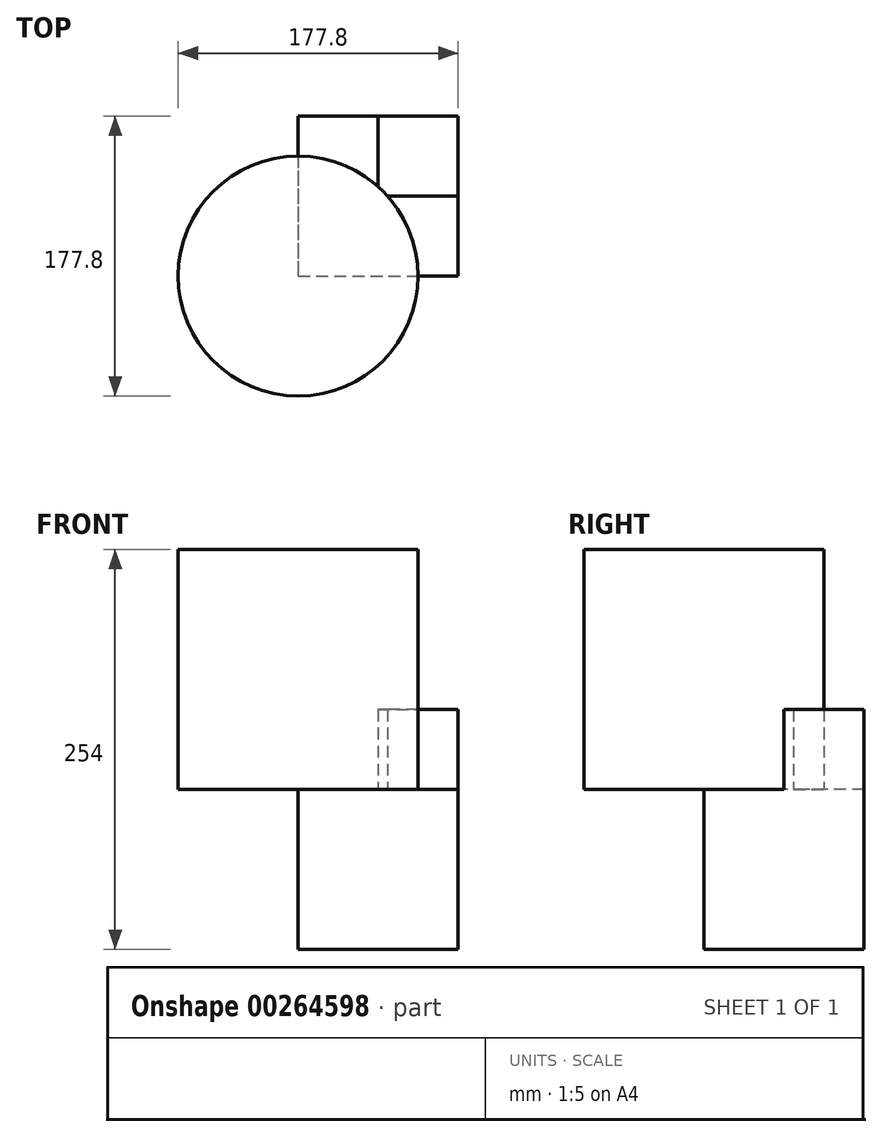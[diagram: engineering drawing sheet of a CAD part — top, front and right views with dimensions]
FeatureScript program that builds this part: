
annotation { "Feature Type Name" : "Feature", "Feature Type Description" : "" }
export const myFeature = defineFeature(function(context is Context, id is Id, definition is map)
    precondition{}
    {
        {
            var Q0;
            Q0=qCreatedBy(makeId("Front.planeOp"),FACE);
            var sketch = newSketch(context, id + "F0", { "sketchPlane" : qUnion([Q0])});
            skLineSegment(sketch, "E0.bottom", {"start": v(0, 0) * mm, "end": v(101.6, 0) * mm});
            skLineSegment(sketch, "E0.top", {"start": v(0, 101.6) * mm, "end": v(101.6, 101.6) * mm});
            skLineSegment(sketch, "E0.left", {"start": v(0, 0) * mm, "end": v(0, 101.6) * mm});
            skLineSegment(sketch, "E0.right", {"start": v(101.6, 0) * mm, "end": v(101.6, 101.6) * mm});
            skSolve(sketch);
        }
        {
            var Q0;
            Q0 = qSketchRegion(id + "F0", true);
            extrude(context, id + "F1", {"entities" : qUnion([Q0]), "oppositeDirection" : true, "depth" : 101.6 * mm});
        }
        {
            var Q0;
            Q0=makeQuery(id+"F1.opExtrude","SWEPT_FACE",FACE,{"disambiguationData":[OSD([sQuery(id+"F0.wireOp",EDGE,"E0.top")])]});
            var sketch = newSketch(context, id + "F2", { "sketchPlane" : qUnion([Q0])});
            skCircle(sketch, "E1", {"center": v(0, 0) * mm, "radius": 76.2 * mm});
            skSolve(sketch);
        }
        {
            var Q0;
            Q0 = qSketchRegion(id + "F2", true);
            extrude(context, id + "F3", {"entities" : qUnion([Q0]), "operationType" : NewBodyOperationType.ADD, "depth" : 152.4 * mm});
        }
        {
            var Q0;
            Q0=makeQuery(id+"F1.opExtrude","SWEPT_FACE",FACE,{"disambiguationData":[OSD([sQuery(id+"F0.wireOp",EDGE,"E0.top")])]});
            var sketch = newSketch(context, id + "F4", { "sketchPlane" : qUnion([Q0])});
            skLineSegment(sketch, "E2.bottom", {"start": v(101.6, 101.6) * mm, "end": v(50.8, 101.6) * mm});
            skLineSegment(sketch, "E2.top", {"start": v(101.6, 50.8) * mm, "end": v(50.8, 50.8) * mm});
            skLineSegment(sketch, "E2.left", {"start": v(101.6, 101.6) * mm, "end": v(101.6, 50.8) * mm});
            skLineSegment(sketch, "E2.right", {"start": v(50.8, 101.6) * mm, "end": v(50.8, 50.8) * mm});
            skSolve(sketch);
        }
        {
            var Q0;
            Q0 = qSketchRegion(id + "F4", true);
            extrude(context, id + "F5", {"entities" : qUnion([Q0]), "operationType" : NewBodyOperationType.ADD, "depth" : 50.8 * mm});
        }
    });
